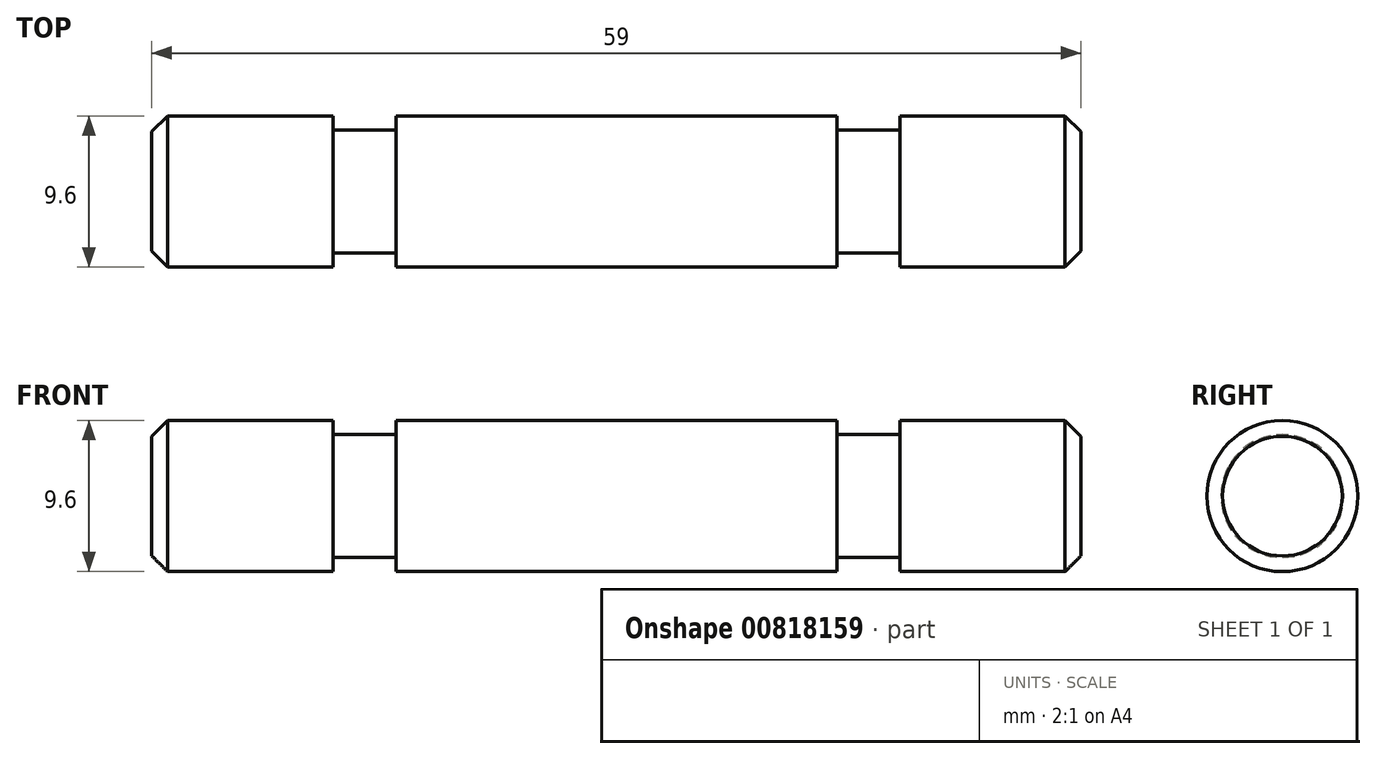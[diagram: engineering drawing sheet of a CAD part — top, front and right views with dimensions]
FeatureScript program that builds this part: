
annotation { "Feature Type Name" : "Feature", "Feature Type Description" : "" }
export const myFeature = defineFeature(function(context is Context, id is Id, definition is map)
    precondition{}
    {
        {
            var Q0;
            Q0=qCreatedBy(makeId("Front.planeOp"),FACE);
            var sketch = newSketch(context, id + "F0", { "sketchPlane" : qUnion([Q0])});
            skLineSegment(sketch, "E0", {"start": v(-29.5, 4.8) * mm, "end": v(-18, 4.8) * mm});
            skLineSegment(sketch, "E1", {"start": v(-18, 4.8) * mm, "end": v(-18, 3.9) * mm});
            skLineSegment(sketch, "E2", {"start": v(-18, 3.9) * mm, "end": v(-14, 3.9) * mm});
            skLineSegment(sketch, "E3", {"start": v(-14, 3.9) * mm, "end": v(-14, 4.8) * mm});
            skLineSegment(sketch, "E4", {"start": v(-14, 4.8) * mm, "end": v(14, 4.8) * mm});
            skLineSegment(sketch, "E5", {"start": v(14, 4.8) * mm, "end": v(14, 3.9) * mm});
            skLineSegment(sketch, "E6", {"start": v(14, 3.9) * mm, "end": v(18, 3.9) * mm});
            skLineSegment(sketch, "E7", {"start": v(18, 3.9) * mm, "end": v(18, 4.8) * mm});
            skLineSegment(sketch, "E8", {"start": v(18, 4.8) * mm, "end": v(29.5, 4.8) * mm});
            skLineSegment(sketch, "E9", {"start": v(29.5, 4.8) * mm, "end": v(29.5, 0) * mm});
            skLineSegment(sketch, "E10", {"start": v(-29.5, 0) * mm, "end": v(29.5, 0) * mm, "construction": true});
            skLineSegment(sketch, "E11.MirrorCS", {"start": v(-29.5, -4.8) * mm, "end": v(-18, -4.8) * mm, "construction": true});
            skLineSegment(sketch, "E12.MirrorCS", {"start": v(-18, -4.8) * mm, "end": v(-18, -3.9) * mm, "construction": true});
            skLineSegment(sketch, "E13.MirrorCS", {"start": v(-18, -3.9) * mm, "end": v(-14, -3.9) * mm, "construction": true});
            skLineSegment(sketch, "E14.MirrorCS", {"start": v(-14, -3.9) * mm, "end": v(-14, -4.8) * mm, "construction": true});
            skLineSegment(sketch, "E15.MirrorCS", {"start": v(-14, -4.8) * mm, "end": v(14, -4.8) * mm, "construction": true});
            skLineSegment(sketch, "E16.MirrorCS", {"start": v(14, -3.9) * mm, "end": v(18, -3.9) * mm, "construction": true});
            skLineSegment(sketch, "E17.MirrorCS", {"start": v(14, -4.8) * mm, "end": v(14, -3.9) * mm, "construction": true});
            skLineSegment(sketch, "E18.MirrorCS", {"start": v(18, -3.9) * mm, "end": v(18, -4.8) * mm, "construction": true});
            skLineSegment(sketch, "E19.MirrorCS", {"start": v(18, -3.9) * mm, "end": v(18, -4.8) * mm});
            skLineSegment(sketch, "E20.MirrorCS", {"start": v(18, -4.8) * mm, "end": v(29.5, -4.8) * mm, "construction": true});
            skLineSegment(sketch, "E21.MirrorCS", {"start": v(29.5, -4.8) * mm, "end": v(29.5, 0) * mm, "construction": true});
            skLineSegment(sketch, "E22", {"start": v(-29.5, 4.8) * mm, "end": v(-29.5, 0) * mm});
            skLineSegment(sketch, "E23", {"start": v(-29.5, -4.8) * mm, "end": v(-29.5, 0) * mm, "construction": true});
            skPoint(sketch, "E24", {"position": v(0, 4.8) * mm});
            skLineSegment(sketch, "E25", {"start": v(-29.5, 0) * mm, "end": v(29.5, 0) * mm});
            skSolve(sketch);
        }
        {
            var Q0;
            Q0=makeQuery(id+"F0.imprint","IMPRINT",FACE,{"disambiguationData":[TD([[makeQuery(id+"F0.imprint","IMPRINT",EDGE,{"derivedFrom":sQuery(id+"F0.wireOp",EDGE,"E0")}),-1.0]])]});
            var Q1;
            Q1=sQuery(id+"F0.wireOp",EDGE,"E9");
            var Q2;
            Q2=sQuery(id+"F0.wireOp",EDGE,"E8");
            var Q3;
            Q3=sQuery(id+"F0.wireOp",EDGE,"E7");
            var Q4;
            Q4=sQuery(id+"F0.wireOp",EDGE,"E6");
            var Q5;
            Q5=sQuery(id+"F0.wireOp",EDGE,"E4");
            var Q6;
            Q6=sQuery(id+"F0.wireOp",EDGE,"E3");
            var Q7;
            Q7=sQuery(id+"F0.wireOp",EDGE,"E2");
            var Q8;
            Q8=sQuery(id+"F0.wireOp",EDGE,"E1");
            var Q9;
            Q9=sQuery(id+"F0.wireOp",EDGE,"E0");
            var Q10;
            Q10=sQuery(id+"F0.wireOp",EDGE,"E22");
            var Q11;
            Q11=sQuery(id+"F0.wireOp",EDGE,"E10");
            revolve(context, id + "F1", {"surfaceOperationType" : NewSurfaceOperationType.NEW, "entities" : qUnion([Q0]), "surfaceEntities" : qUnion([Q1, Q2, Q3, Q4, Q5, Q6, Q7, Q8, Q9, Q10]), "axis" : qUnion([Q11]), "revolveType" : RevolveType.FULL});
        }
        {
            var Q0;
            Q0=makeQuery(id+"F1.opRevolve","SWEPT_EDGE",EDGE,{"disambiguationData":[OSD([sQuery(id+"F0.wireOp",EDGE,"E0"),sQuery(id+"F0.wireOp",EDGE,"E22")])]});
            var Q1;
            Q1=makeQuery(id+"F1.opRevolve","SWEPT_FACE",FACE,{"disambiguationData":[OSD([sQuery(id+"F0.wireOp",EDGE,"E9")])]});
            chamfer(context, id + "F2", {"entities" : qUnion([Q0, Q1]), "width" : 1 * mm, "tangentPropagation" : true});
        }
    });
